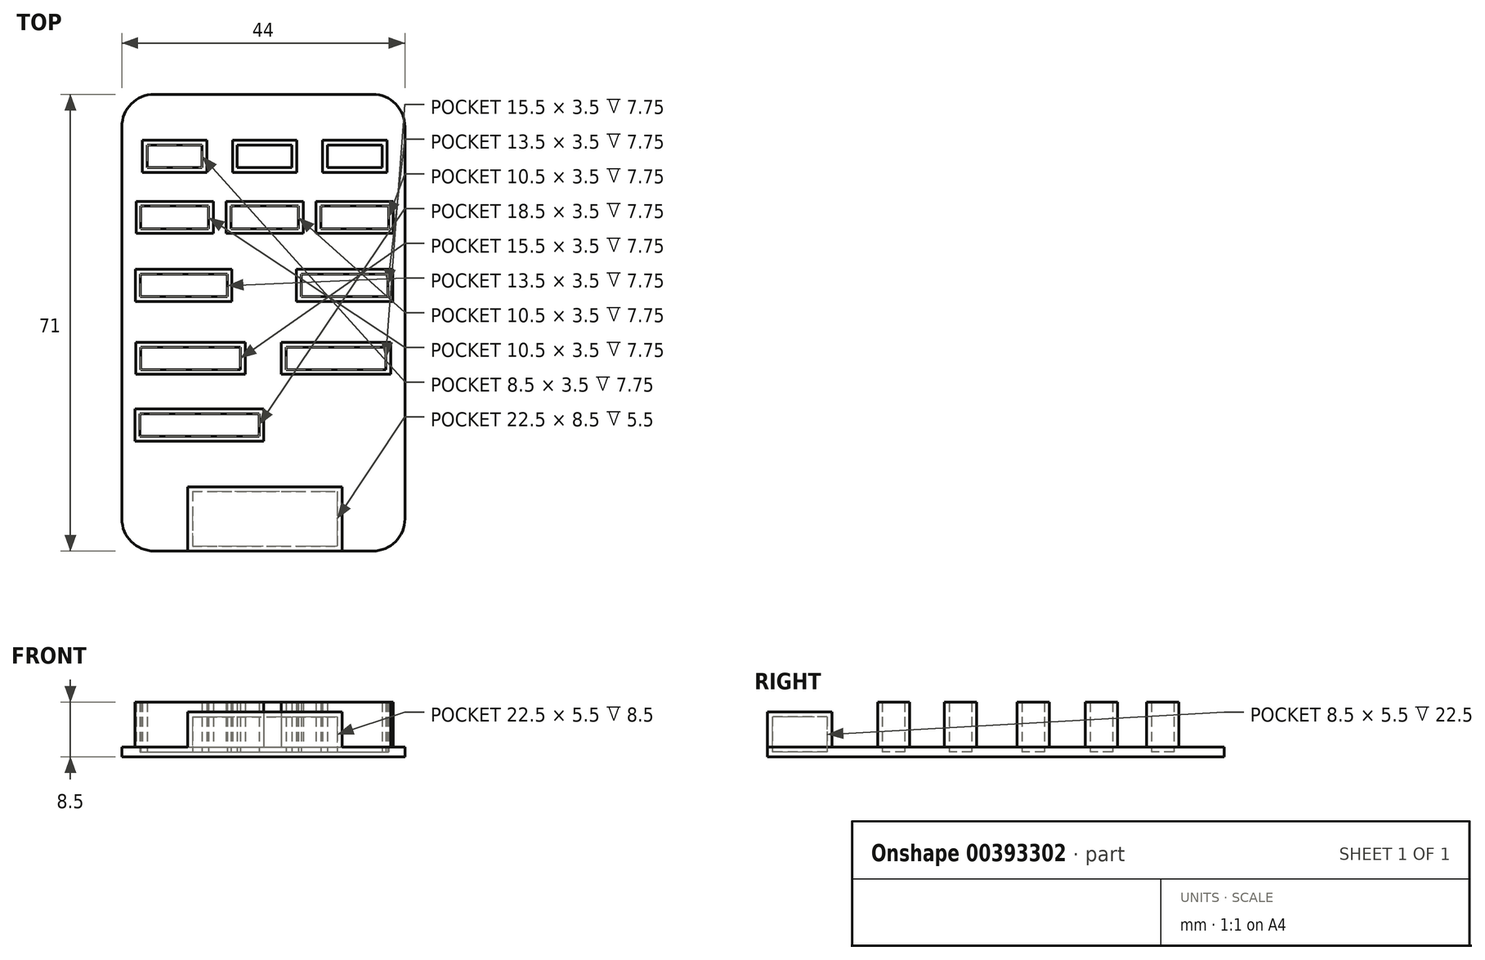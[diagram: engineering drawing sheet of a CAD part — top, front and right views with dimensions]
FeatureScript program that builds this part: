
annotation { "Feature Type Name" : "Feature", "Feature Type Description" : "" }
export const myFeature = defineFeature(function(context is Context, id is Id, definition is map)
    precondition{}
    {
        {
            var Q0;
            Q0=qCreatedBy(makeId("Top.planeOp"),FACE);
            var sketch = newSketch(context, id + "F0", { "sketchPlane" : qUnion([Q0])});
            skLineSegment(sketch, "E0.bottom", {"start": v(-22.5, 37.87) * mm, "end": v(21.5, 37.87) * mm});
            skLineSegment(sketch, "E0.top", {"start": v(-22.5, -33.13) * mm, "end": v(21.5, -33.13) * mm});
            skLineSegment(sketch, "E0.left", {"start": v(-22.5, 37.87) * mm, "end": v(-22.5, -33.13) * mm});
            skLineSegment(sketch, "E0.right", {"start": v(21.5, 37.87) * mm, "end": v(21.5, -33.13) * mm});
            skSolve(sketch);
        }
        {
            var Q0;
            Q0=makeQuery(id+"F0.imprint","IMPRINT",FACE,{"disambiguationData":[TD([[makeQuery(id+"F0.imprint","IMPRINT",EDGE,{"derivedFrom":sQuery(id+"F0.wireOp",EDGE,"E0.bottom")}),-1.0]])]});
            extrude(context, id + "F1", {"entities" : qUnion([Q0]), "depth" : 1.5 * mm});
        }
        {
            var Q0;
            Q0=makeQuery(id+"F1.opExtrude","SWEPT_EDGE",EDGE,{"disambiguationData":[OSD([sQuery(id+"F0.wireOp",EDGE,"E0.bottom"),sQuery(id+"F0.wireOp",EDGE,"E0.left")])]});
            var Q1;
            Q1=makeQuery(id+"F1.opExtrude","SWEPT_EDGE",EDGE,{"disambiguationData":[OSD([sQuery(id+"F0.wireOp",EDGE,"E0.top"),sQuery(id+"F0.wireOp",EDGE,"E0.left")])]});
            var Q2;
            Q2=makeQuery(id+"F1.opExtrude","SWEPT_EDGE",EDGE,{"disambiguationData":[OSD([sQuery(id+"F0.wireOp",EDGE,"E0.top"),sQuery(id+"F0.wireOp",EDGE,"E0.right")])]});
            var Q3;
            Q3=makeQuery(id+"F1.opExtrude","SWEPT_EDGE",EDGE,{"disambiguationData":[OSD([sQuery(id+"F0.wireOp",EDGE,"E0.bottom"),sQuery(id+"F0.wireOp",EDGE,"E0.right")])]});
            fillet(context, id + "F2", {"entities" : qUnion([Q0, Q1, Q2, Q3]), "radius" : 5 * mm, "tangentPropagation" : true, "allowEdgeOverflow" : false});
        }
        {
            var Q0;
            Q0=makeQuery(id+"F1.opExtrude","CAP_FACE",FACE,{"disambiguationData":[OSD([sQuery(id+"F0.wireOp",EDGE,"E0.bottom"),sQuery(id+"F0.wireOp",EDGE,"E0.top"),sQuery(id+"F0.wireOp",EDGE,"E0.left"),sQuery(id+"F0.wireOp",EDGE,"E0.right")])],"isStart":false});
            var sketch = newSketch(context, id + "F3", { "sketchPlane" : qUnion([Q0])});
            skLineSegment(sketch, "E1.bottom", {"start": v(-12.28, -23.13) * mm, "end": v(11.72, -23.13) * mm});
            skLineSegment(sketch, "E1.top", {"start": v(-12.28, -33.13) * mm, "end": v(11.72, -33.13) * mm});
            skLineSegment(sketch, "E1.left", {"start": v(-12.28, -23.13) * mm, "end": v(-12.28, -33.13) * mm});
            skLineSegment(sketch, "E1.right", {"start": v(11.72, -23.13) * mm, "end": v(11.72, -33.13) * mm});
            skSolve(sketch);
        }
        {
            var Q0;
            Q0 = qSketchRegion(id + "F3", true);
            extrude(context, id + "F4", {"entities" : qUnion([Q0]), "operationType" : NewBodyOperationType.ADD, "depth" : 5.5 * mm});
        }
        {
            var Q0;
            Q0=makeQuery(id+"F3.imprint","IMPRINT",FACE,{"disambiguationData":[TD([[makeQuery(id+"F3.imprint","IMPRINT",EDGE,{"derivedFrom":sQuery(id+"F3.wireOp",EDGE,"E1.bottom")}),1.0]])]});
            var sketch = newSketch(context, id + "F5", { "sketchPlane" : qUnion([Q0])});
            skLineSegment(sketch, "E2.bottom", {"start": v(-19.3, 30.77) * mm, "end": v(-9.3, 30.77) * mm});
            skLineSegment(sketch, "E2.top", {"start": v(-19.3, 25.77) * mm, "end": v(-9.3, 25.77) * mm});
            skLineSegment(sketch, "E2.left", {"start": v(-19.3, 30.77) * mm, "end": v(-19.3, 25.77) * mm});
            skLineSegment(sketch, "E2.right", {"start": v(-9.3, 30.77) * mm, "end": v(-9.3, 25.77) * mm});
            skLineSegment(sketch, "E3.1.0.0", {"start": v(-5.3, 30.77) * mm, "end": v(4.7, 30.77) * mm});
            skLineSegment(sketch, "E3.1.0.1", {"start": v(4.7, 30.77) * mm, "end": v(4.7, 25.77) * mm});
            skLineSegment(sketch, "E3.1.0.2", {"start": v(-5.3, 25.77) * mm, "end": v(4.7, 25.77) * mm});
            skLineSegment(sketch, "E3.1.0.3", {"start": v(-5.3, 30.77) * mm, "end": v(-5.3, 25.77) * mm});
            skLineSegment(sketch, "E3.2.0.0", {"start": v(8.7, 30.77) * mm, "end": v(18.7, 30.77) * mm});
            skLineSegment(sketch, "E3.2.0.1", {"start": v(18.7, 30.77) * mm, "end": v(18.7, 25.77) * mm});
            skLineSegment(sketch, "E3.2.0.2", {"start": v(8.7, 25.77) * mm, "end": v(18.7, 25.77) * mm});
            skLineSegment(sketch, "E3.2.0.3", {"start": v(8.7, 30.77) * mm, "end": v(8.7, 25.77) * mm});
            skLineSegment(sketch, "E4.bottom", {"start": v(-20.3, 21.25) * mm, "end": v(-8.3, 21.25) * mm});
            skLineSegment(sketch, "E4.top", {"start": v(-20.3, 16.25) * mm, "end": v(-8.3, 16.25) * mm});
            skLineSegment(sketch, "E4.left", {"start": v(-20.3, 21.25) * mm, "end": v(-20.3, 16.25) * mm});
            skLineSegment(sketch, "E4.right", {"start": v(-8.3, 21.25) * mm, "end": v(-8.3, 16.25) * mm});
            skLineSegment(sketch, "E5.1.0.0", {"start": v(-6.3, 21.25) * mm, "end": v(5.7, 21.25) * mm});
            skLineSegment(sketch, "E5.1.0.1", {"start": v(5.7, 21.25) * mm, "end": v(5.7, 16.25) * mm});
            skLineSegment(sketch, "E5.1.0.2", {"start": v(-6.3, 16.25) * mm, "end": v(5.7, 16.25) * mm});
            skLineSegment(sketch, "E5.1.0.3", {"start": v(-6.3, 21.25) * mm, "end": v(-6.3, 16.25) * mm});
            skLineSegment(sketch, "E5.2.0.0", {"start": v(7.7, 21.25) * mm, "end": v(19.7, 21.25) * mm});
            skLineSegment(sketch, "E5.2.0.1", {"start": v(19.7, 21.25) * mm, "end": v(19.7, 16.25) * mm});
            skLineSegment(sketch, "E5.2.0.2", {"start": v(7.7, 16.25) * mm, "end": v(19.7, 16.25) * mm});
            skLineSegment(sketch, "E5.2.0.3", {"start": v(7.7, 21.25) * mm, "end": v(7.7, 16.25) * mm});
            skLineSegment(sketch, "E6.bottom", {"start": v(-20.39, 10.66) * mm, "end": v(-5.39, 10.66) * mm});
            skLineSegment(sketch, "E6.top", {"start": v(-20.39, 5.66) * mm, "end": v(-5.39, 5.66) * mm});
            skLineSegment(sketch, "E6.left", {"start": v(-20.39, 10.66) * mm, "end": v(-20.39, 5.66) * mm});
            skLineSegment(sketch, "E6.right", {"start": v(-5.39, 10.66) * mm, "end": v(-5.39, 5.66) * mm});
            skLineSegment(sketch, "E7.bottom", {"start": v(-20.33, -0.66) * mm, "end": v(-3.33, -0.66) * mm});
            skLineSegment(sketch, "E7.top", {"start": v(-20.33, -5.66) * mm, "end": v(-3.33, -5.66) * mm});
            skLineSegment(sketch, "E7.left", {"start": v(-20.33, -0.66) * mm, "end": v(-20.33, -5.66) * mm});
            skLineSegment(sketch, "E7.right", {"start": v(-3.33, -0.66) * mm, "end": v(-3.33, -5.66) * mm});
            skLineSegment(sketch, "E8.bottom", {"start": v(-20.44, -11.03) * mm, "end": v(-0.44, -11.03) * mm});
            skLineSegment(sketch, "E8.top", {"start": v(-20.44, -16.03) * mm, "end": v(-0.44, -16.03) * mm});
            skLineSegment(sketch, "E8.left", {"start": v(-20.44, -11.03) * mm, "end": v(-20.44, -16.03) * mm});
            skLineSegment(sketch, "E8.right", {"start": v(-0.44, -11.03) * mm, "end": v(-0.44, -16.03) * mm});
            skLineSegment(sketch, "E9.1.0.0", {"start": v(4.61, 10.66) * mm, "end": v(4.61, 5.66) * mm});
            skLineSegment(sketch, "E9.1.0.1", {"start": v(4.61, 10.66) * mm, "end": v(19.61, 10.66) * mm});
            skLineSegment(sketch, "E9.1.0.2", {"start": v(19.61, 10.66) * mm, "end": v(19.61, 5.66) * mm});
            skLineSegment(sketch, "E9.1.0.3", {"start": v(4.61, 5.66) * mm, "end": v(19.61, 5.66) * mm});
            skLineSegment(sketch, "E9.direction1", {"start": v(-20.39, 5.66) * mm, "end": v(4.61, 5.66) * mm, "construction": true});
            skLineSegment(sketch, "E10.1.0.0", {"start": v(2.27, -0.66) * mm, "end": v(2.27, -5.66) * mm});
            skLineSegment(sketch, "E10.1.0.1", {"start": v(2.27, -0.66) * mm, "end": v(19.27, -0.66) * mm});
            skLineSegment(sketch, "E10.1.0.2", {"start": v(19.27, -0.66) * mm, "end": v(19.27, -5.66) * mm});
            skLineSegment(sketch, "E10.1.0.3", {"start": v(2.27, -5.66) * mm, "end": v(19.27, -5.66) * mm});
            skLineSegment(sketch, "E10.direction1", {"start": v(-20.33, -5.66) * mm, "end": v(2.27, -5.66) * mm, "construction": true});
            skSolve(sketch);
        }
        {
            var Q0;
            Q0=makeQuery(id+"F5.imprint","IMPRINT",FACE,{"disambiguationData":[TD([[makeQuery(id+"F5.imprint","IMPRINT",EDGE,{"derivedFrom":sQuery(id+"F5.wireOp",EDGE,"E2.bottom")}),-1.0]])]});
            var Q1;
            Q1=makeQuery(id+"F5.imprint","IMPRINT",FACE,{"disambiguationData":[TD([[makeQuery(id+"F5.imprint","IMPRINT",EDGE,{"derivedFrom":sQuery(id+"F5.wireOp",EDGE,"E3.1.0.0")}),-1.0]])]});
            var Q2;
            Q2=makeQuery(id+"F5.imprint","IMPRINT",FACE,{"disambiguationData":[TD([[makeQuery(id+"F5.imprint","IMPRINT",EDGE,{"derivedFrom":sQuery(id+"F5.wireOp",EDGE,"E3.2.0.0")}),-1.0]])]});
            var Q3;
            Q3=makeQuery(id+"F5.imprint","IMPRINT",FACE,{"disambiguationData":[TD([[makeQuery(id+"F5.imprint","IMPRINT",EDGE,{"derivedFrom":sQuery(id+"F5.wireOp",EDGE,"E4.bottom")}),-1.0]])]});
            var Q4;
            Q4=makeQuery(id+"F5.imprint","IMPRINT",FACE,{"disambiguationData":[TD([[makeQuery(id+"F5.imprint","IMPRINT",EDGE,{"derivedFrom":sQuery(id+"F5.wireOp",EDGE,"E5.1.0.0")}),-1.0]])]});
            var Q5;
            Q5=makeQuery(id+"F5.imprint","IMPRINT",FACE,{"disambiguationData":[TD([[makeQuery(id+"F5.imprint","IMPRINT",EDGE,{"derivedFrom":sQuery(id+"F5.wireOp",EDGE,"E6.bottom")}),-1.0]])]});
            var Q6;
            Q6=makeQuery(id+"F5.imprint","IMPRINT",FACE,{"disambiguationData":[TD([[makeQuery(id+"F5.imprint","IMPRINT",EDGE,{"derivedFrom":sQuery(id+"F5.wireOp",EDGE,"E7.bottom")}),-1.0]])]});
            var Q7;
            Q7=makeQuery(id+"F5.imprint","IMPRINT",FACE,{"disambiguationData":[TD([[makeQuery(id+"F5.imprint","IMPRINT",EDGE,{"derivedFrom":sQuery(id+"F5.wireOp",EDGE,"E8.bottom")}),-1.0]])]});
            var Q8;
            Q8=makeQuery(id+"F5.imprint","IMPRINT",FACE,{"disambiguationData":[TD([[makeQuery(id+"F5.imprint","IMPRINT",EDGE,{"derivedFrom":sQuery(id+"F5.wireOp",EDGE,"E5.2.0.0")}),-1.0]])]});
            var Q9;
            Q9=makeQuery(id+"F5.imprint","IMPRINT",FACE,{"disambiguationData":[TD([[makeQuery(id+"F5.imprint","IMPRINT",EDGE,{"derivedFrom":sQuery(id+"F5.wireOp",EDGE,"E9.1.0.0")}),1.0]])]});
            var Q10;
            Q10=makeQuery(id+"F5.imprint","IMPRINT",FACE,{"disambiguationData":[TD([[makeQuery(id+"F5.imprint","IMPRINT",EDGE,{"derivedFrom":sQuery(id+"F5.wireOp",EDGE,"E10.1.0.0")}),1.0]])]});
            extrude(context, id + "F6", {"entities" : qUnion([Q0, Q1, Q2, Q3, Q4, Q5, Q6, Q7, Q8, Q9, Q10]), "operationType" : NewBodyOperationType.ADD, "depth" : 7 * mm});
        }
        {
            var Q0;
            Q0=makeQuery(id+"F6.opExtrude","CAP_FACE",FACE,{"disambiguationData":[OSD([sQuery(id+"F5.wireOp",EDGE,"E2.bottom"),sQuery(id+"F5.wireOp",EDGE,"E2.top"),sQuery(id+"F5.wireOp",EDGE,"E2.left"),sQuery(id+"F5.wireOp",EDGE,"E2.right")])],"isStart":false});
            var Q1;
            Q1=makeQuery(id+"F6.opExtrude","CAP_FACE",FACE,{"disambiguationData":[OSD([sQuery(id+"F5.wireOp",EDGE,"E3.1.0.0"),sQuery(id+"F5.wireOp",EDGE,"E3.1.0.1"),sQuery(id+"F5.wireOp",EDGE,"E3.1.0.2"),sQuery(id+"F5.wireOp",EDGE,"E3.1.0.3")])],"isStart":false});
            var Q2;
            Q2=makeQuery(id+"F6.opExtrude","CAP_FACE",FACE,{"disambiguationData":[OSD([sQuery(id+"F5.wireOp",EDGE,"E3.2.0.0"),sQuery(id+"F5.wireOp",EDGE,"E3.2.0.1"),sQuery(id+"F5.wireOp",EDGE,"E3.2.0.2"),sQuery(id+"F5.wireOp",EDGE,"E3.2.0.3")])],"isStart":false});
            var Q3;
            Q3=makeQuery(id+"F6.opExtrude","CAP_FACE",FACE,{"disambiguationData":[OSD([sQuery(id+"F5.wireOp",EDGE,"E5.2.0.0"),sQuery(id+"F5.wireOp",EDGE,"E5.2.0.1"),sQuery(id+"F5.wireOp",EDGE,"E5.2.0.2"),sQuery(id+"F5.wireOp",EDGE,"E5.2.0.3")])],"isStart":false});
            var Q4;
            Q4=makeQuery(id+"F6.opExtrude","CAP_FACE",FACE,{"disambiguationData":[OSD([sQuery(id+"F5.wireOp",EDGE,"E9.1.0.0"),sQuery(id+"F5.wireOp",EDGE,"E9.1.0.1"),sQuery(id+"F5.wireOp",EDGE,"E9.1.0.2"),sQuery(id+"F5.wireOp",EDGE,"E9.1.0.3")])],"isStart":false});
            var Q5;
            Q5=makeQuery(id+"F6.opExtrude","CAP_FACE",FACE,{"disambiguationData":[OSD([sQuery(id+"F5.wireOp",EDGE,"E6.bottom"),sQuery(id+"F5.wireOp",EDGE,"E6.top"),sQuery(id+"F5.wireOp",EDGE,"E6.left"),sQuery(id+"F5.wireOp",EDGE,"E6.right")])],"isStart":false});
            var Q6;
            Q6=makeQuery(id+"F6.opExtrude","CAP_FACE",FACE,{"disambiguationData":[OSD([sQuery(id+"F5.wireOp",EDGE,"E4.bottom"),sQuery(id+"F5.wireOp",EDGE,"E4.top"),sQuery(id+"F5.wireOp",EDGE,"E4.left"),sQuery(id+"F5.wireOp",EDGE,"E4.right")])],"isStart":false});
            var Q7;
            Q7=makeQuery(id+"F6.opExtrude","CAP_FACE",FACE,{"disambiguationData":[OSD([sQuery(id+"F5.wireOp",EDGE,"E5.1.0.0"),sQuery(id+"F5.wireOp",EDGE,"E5.1.0.1"),sQuery(id+"F5.wireOp",EDGE,"E5.1.0.2"),sQuery(id+"F5.wireOp",EDGE,"E5.1.0.3")])],"isStart":false});
            var Q8;
            Q8=makeQuery(id+"F6.opExtrude","CAP_FACE",FACE,{"disambiguationData":[OSD([sQuery(id+"F5.wireOp",EDGE,"E10.1.0.0"),sQuery(id+"F5.wireOp",EDGE,"E10.1.0.1"),sQuery(id+"F5.wireOp",EDGE,"E10.1.0.2"),sQuery(id+"F5.wireOp",EDGE,"E10.1.0.3")])],"isStart":false});
            var Q9;
            Q9=makeQuery(id+"F6.opExtrude","CAP_FACE",FACE,{"disambiguationData":[OSD([sQuery(id+"F5.wireOp",EDGE,"E7.bottom"),sQuery(id+"F5.wireOp",EDGE,"E7.top"),sQuery(id+"F5.wireOp",EDGE,"E7.left"),sQuery(id+"F5.wireOp",EDGE,"E7.right")])],"isStart":false});
            var Q10;
            Q10=makeQuery(id+"F6.opExtrude","CAP_FACE",FACE,{"disambiguationData":[OSD([sQuery(id+"F5.wireOp",EDGE,"E8.bottom"),sQuery(id+"F5.wireOp",EDGE,"E8.top"),sQuery(id+"F5.wireOp",EDGE,"E8.left"),sQuery(id+"F5.wireOp",EDGE,"E8.right")])],"isStart":false});
            shell(context, id + "F7", {"entities" : qUnion([Q0, Q1, Q2, Q3, Q4, Q5, Q6, Q7, Q8, Q9, Q10]), "thickness" : 0.75 * mm});
        }
    });
